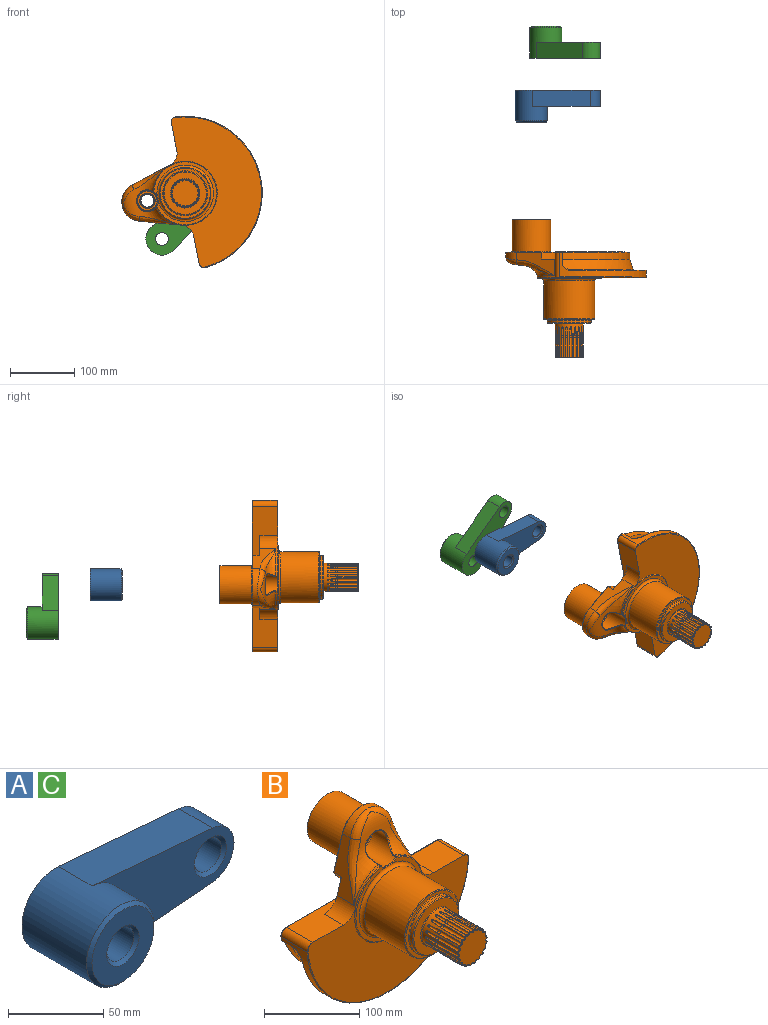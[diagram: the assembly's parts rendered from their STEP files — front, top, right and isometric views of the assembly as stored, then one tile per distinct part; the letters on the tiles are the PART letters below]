
ASSEMBLY  parts=3 mates=2
PART A: 12 faces, bbox 132.5x50x50 mm
  f0: plane 105.42x49.83mm, normal (0,-1,0), area 2885.2mm2, adj f1,f2,f3,f4,f9
  f1: cylinder r=25mm len=50mm, axis (0,1,0), area 5680.6mm2, adj f0,f2,f4,f7,f11
  f2: plane 89.38x25mm, normal (0.08,0,-1), area 2242.2mm2, adj f0,f1,f3,f7
  f3: cylinder r=17.5mm len=34.88mm, axis (0,1,0), area 1301.4mm2, adj f0,f2,f4,f7
  f4: plane 89.38x25mm, normal (0.08,0,1), area 2242.2mm2, adj f0,f1,f3,f7
  f5: cylinder r=10mm len=48mm, axis (0,1,0), area 3015.9mm2, adj f7,f10
  f6: cylinder r=10mm len=23mm, axis (0,1,0), area 1445.1mm2, adj f7,f9
  f7: plane 132.5x50mm, normal (0,1,0), area 4672.8mm2, adj f1,f2,f3,f4,f5,f6
  f8: plane 46x46mm, normal (0,-1,0), area 1209.5mm2, adj f10,f11
  f9: cone r=10mm half-angle=45deg, axis (0,-1,0), area 195.5mm2, adj f0,f6
  f10: cone r=10mm half-angle=45deg, axis (0,-1,0), area 195.5mm2, adj f5,f8
  f11: cone r=23mm half-angle=45deg, axis (0,1,0), area 426.5mm2, adj f1,f8
PART B: 359 faces, bbox 259.9x215.3x232.7 mm
  f0: cylinder r=22mm len=52mm, axis (0,-1,0), area 3266.6mm2, adj f52,f159,f162,f163,f166,f167,f170,f171
  f1: plane 42.73x42.73mm, normal (0,-1,0), area 1310mm2, adj f159,f160,f161,f162,f163,f164,f165,f166
  f2: cylinder r=50mm len=36.05mm, axis (0,1,0), area 156.2mm2, adj f19,f32,f44,f45
  f3: plane 237.43x92mm, normal (0,1,0), area 16224.2mm2, adj f60,f61,f62,f63,f64,f65,f66,f67
  f4: plane 98x96.6mm, normal (0,-1,0), area 1372.1mm2, adj f39,f40,f43,f44
  f5: plane 64.61x36.32mm, normal (-0.96,0,0.29), area 1116.4mm2, adj f6,f30,f31,f33,f34,f68,f71
  f6: cylinder r=30mm len=57.5mm, axis (0,-1,0), area 712.7mm2, adj f5,f7,f35,f69
  f7: plane 64.61x36.32mm, normal (0.96,0,0.29), area 1116.4mm2, adj f6,f30,f31,f32,f36,f68,f70
  f8: cylinder r=50mm len=36.05mm, axis (0,1,0), area 156.2mm2, adj f19,f33,f44,f48
  f9: plane 86.65x81.31mm, normal (0,1,0), area 2091.3mm2, adj f69,f70,f71,f72,f78
  f10: plane 223.43x39mm, normal (0,0,1), area 4957.1mm2, adj f11,f30,f32,f33,f37,f38,f65
  f11: plane 237.83x133.29mm, normal (0,-1,0), area 18403mm2, adj f10,f32,f33,f37,f38,f44,f53
  f12: cylinder r=120mm len=239.39mm, axis (0,-1,0), area 3826.2mm2, adj f27,f28,f37,f38,f53,f54,f55,f56
  f13: cylinder r=40mm len=80mm, axis (0,-1,0), area 14828.3mm2, adj f39,f49
  f14: plane 78x78mm, normal (0,-1,0), area 929.9mm2, adj f49,f50
  f15: cylinder r=34mm len=68mm, axis (0,-1,0), area 854.5mm2, adj f50,f51
  f16: plane 66x66mm, normal (0,-1,0), area 1759.3mm2, adj f51,f52
  f17: cylinder r=30mm len=60mm, axis (0,-1,0), area 9236.3mm2, adj f18,f78
  f18: plane 60x60mm, normal (0,1,0), area 1306.9mm2, adj f17,f76
  f19: revolved ~188.29x83.96mm, area 2110.2mm2, adj f2,f8,f34,f35,f36,f47
  f20: cylinder r=21mm len=42mm, axis (0,1,0), area 3034.8mm2, adj f76,f77
  f21: plane 40x40mm, normal (0,1,0), area 804.2mm2, adj f75,f77
  f22: cylinder r=11mm len=23mm, axis (0,1,0), area 1589.6mm2, adj f73,f75
  f23: cylinder r=16mm len=39mm, axis (0,1,0), area 2594.1mm2, adj f40,f41,f43,f45,f47,f48,f74
  f24: plane 30x30mm, normal (0,-1,0), area 254.5mm2, adj f73,f74
  f25: cone r=124mm half-angle=17deg, axis (0,-1,0), area 4998.2mm2, adj f27,f28,f29,f54,f57,f59
  f26: plane 230.56x89.48mm, normal (0,1,0), area 3734.6mm2, adj f56,f57
  f27: plane 20.74x2.73mm, normal (0.34,0,-0.94), area 45.7mm2, adj f12,f25,f29,f59,f60
  f28: plane 20.74x2.73mm, normal (-0.34,0,-0.94), area 45.7mm2, adj f12,f25,f29,f54,f64
  f29: cylinder r=124mm len=233.04mm, axis (0,-1,0), area 3332.9mm2, adj f25,f27,f28,f62
  f30: plane 134.16x33.71mm, normal (0,1,0), area 1873mm2, adj f5,f7,f10,f32,f33,f68
  f31: cylinder r=48.65mm len=83.48mm, axis (0,1,0), area 1003.4mm2, adj f5,f7,f68,f72
  f32: cylinder r=20mm len=28mm, axis (0,1,0), area 717.4mm2, adj f2,f7,f10,f11,f30
  f33: cylinder r=20mm len=28mm, axis (0,1,0), area 717.4mm2, adj f5,f8,f10,f11,f30
  f34: bspline ~68.35x27.48mm, area 558mm2, adj f5,f19,f35
  f35: bspline ~59.09x25.38mm, area 693.8mm2, adj f6,f19,f34,f36
  f36: bspline ~68.35x27.48mm, area 558mm2, adj f7,f19,f35
  f37: cylinder r=8mm len=39mm, axis (0,-1,0), area 510.3mm2, adj f10,f11,f12,f53,f67
  f38: cylinder r=8mm len=39mm, axis (0,-1,0), area 510.3mm2, adj f10,f11,f12,f53,f63
  f39: torus R=44mm, axis (0,-1,0), area 1631.2mm2, adj f4,f13,f41
  f40: torus R=17mm, axis (0,-1,0), area 11.8mm2, adj f4,f23,f41,f42
  f41: bspline ~12.15x1.91mm, area 13.8mm2, adj f23,f39,f40,f43
  f42: sphere r=1mm, area 1mm2, adj f40,f44,f45
  f43: torus R=17mm, axis (0,-1,0), area 11.8mm2, adj f4,f23,f41,f46
  f44: torus R=49mm, axis (0,-1,0), area 452.5mm2, adj f2,f4,f8,f11,f42,f46
  f45: cylinder r=1mm len=3mm, axis (0,1,0), area 3mm2, adj f2,f23,f42,f47
  f46: sphere r=1mm, area 1mm2, adj f43,f44,f48
  f47: bspline ~34.26x28.77mm, area 141.2mm2, adj f19,f23,f45,f48
  f48: cylinder r=1mm len=3mm, axis (0,-1,0), area 3mm2, adj f8,f23,f46,f47
  f49: torus R=39mm, axis (0,1,0), area 391.2mm2, adj f13,f14
  f50: torus R=35mm, axis (0,1,0), area 339.2mm2, adj f14,f15
  f51: torus R=33mm, axis (0,1,0), area 332mm2, adj f15,f16
  f52: torus R=23mm, axis (0,1,0), area 220.7mm2, adj f0,f16
  f53: torus R=119mm, axis (0,-1,0), area 569.8mm2, adj f11,f12,f37,f38
  f54: bspline ~21.98x16.93mm, area 3.9mm2, adj f12,f25,f28,f55
  f55: bspline ~11.03x3.76mm, area 8.9mm2, adj f12,f54,f56,f57
  f56: torus R=119mm, axis (0,-1,0), area 496.1mm2, adj f12,f26,f55,f58
  f57: torus R=129.74mm, axis (0,-1,0), area 370.6mm2, adj f25,f26,f55,f58
  f58: bspline ~9.6x3.23mm, area 8.9mm2, adj f12,f56,f57,f59
  f59: bspline ~21.98x16.93mm, area 3.9mm2, adj f12,f25,f27,f58
  f60: cylinder r=1mm len=4.01mm, axis (-0.94,0,-0.34), area 4.3mm2, adj f3,f27,f61,f62
  f61: torus R=119mm, axis (0,-1,0), area 6.6mm2, adj f3,f12,f60,f63
  f62: torus R=123mm, axis (0,-1,0), area 476.1mm2, adj f3,f29,f60,f64
  f63: torus R=7mm, axis (0,-1,0), area 19.7mm2, adj f3,f38,f61,f65
  f64: cylinder r=1mm len=4.01mm, axis (-0.94,0,0.34), area 4.3mm2, adj f3,f28,f62,f66
  f65: cylinder r=1mm len=223.43mm, axis (-1,0,0), area 351mm2, adj f3,f10,f63,f67
  f66: torus R=119mm, axis (0,-1,0), area 6.6mm2, adj f3,f12,f64,f67
  f67: torus R=7mm, axis (0,-1,0), area 19.7mm2, adj f3,f37,f65,f66
  f68: torus R=49.65mm, axis (0,-1,0), area 157.4mm2, adj f5,f7,f30,f31
  f69: torus R=29mm, axis (0,-1,0), area 119.3mm2, adj f6,f9,f70,f71
  f70: cylinder r=1mm len=43.86mm, axis (-0.29,0,0.96), area 71.1mm2, adj f7,f9,f69,f72
  f71: cylinder r=1mm len=43.86mm, axis (-0.29,0,-0.96), area 71.1mm2, adj f5,f9,f69,f72
  f72: torus R=47.65mm, axis (0,-1,0), area 155.7mm2, adj f9,f31,f70,f71
  f73: torus R=12mm, axis (0,1,0), area 112.2mm2, adj f22,f24
  f74: torus R=15mm, axis (0,1,0), area 154.3mm2, adj f23,f24
  f75: torus R=12mm, axis (0,1,0), area 112.2mm2, adj f21,f22
  f76: torus R=22mm, axis (0,1,0), area 210.8mm2, adj f18,f20
  f77: torus R=20mm, axis (0,1,0), area 203.7mm2, adj f20,f21
  f78: torus R=31mm, axis (0,-1,0), area 299.7mm2, adj f9,f17
  f79: revolved ~3.95x3.33mm, area 18.4mm2, adj f80,f82,f354,f355
  f80: cone r=1.06mm half-angle=3.8deg, axis (0,-1,0), area 50.6mm2, adj f79,f81,f356,f357
  f81: torus R=0.06mm, axis (0,1,0), area 2.6mm2, adj f80,f358
  f82: cylinder r=2mm len=30.28mm, axis (0,1,0), area 170.6mm2, adj f79,f351,f352,f353
  f83: revolved ~3.78x3.33mm, area 18.4mm2, adj f84,f86,f346,f347
  f84: cone r=1.06mm half-angle=3.8deg, axis (0,-1,0), area 50.6mm2, adj f83,f85,f348,f349
  f85: torus R=0.06mm, axis (0,1,0), area 2.6mm2, adj f84,f350
  f86: cylinder r=2mm len=30.28mm, axis (0,1,0), area 170.6mm2, adj f83,f343,f344,f345
  f87: revolved ~3.41x3.33mm, area 18.4mm2, adj f88,f90,f338,f339
  f88: cone r=1.06mm half-angle=3.8deg, axis (0,-1,0), area 50.6mm2, adj f87,f89,f340,f341
  f89: torus R=0.06mm, axis (0,1,0), area 2.6mm2, adj f88,f342
  f90: cylinder r=2mm len=30.28mm, axis (0,1,0), area 170.6mm2, adj f87,f335,f336,f337
  f91: revolved ~3.41x3.33mm, area 18.4mm2, adj f92,f94,f330,f331
  f92: cone r=1.06mm half-angle=3.8deg, axis (0,-1,0), area 50.6mm2, adj f91,f93,f332,f333
  f93: torus R=0.06mm, axis (0,1,0), area 2.6mm2, adj f92,f334
  f94: cylinder r=2mm len=30.28mm, axis (0,1,0), area 170.6mm2, adj f91,f327,f328,f329
  f95: revolved ~3.78x3.33mm, area 18.4mm2, adj f96,f98,f322,f323
  f96: cone r=1.06mm half-angle=3.8deg, axis (0,-1,0), area 50.6mm2, adj f95,f97,f324,f325
  f97: torus R=0.06mm, axis (0,1,0), area 2.6mm2, adj f96,f326
  f98: cylinder r=2mm len=30.28mm, axis (0,1,0), area 170.6mm2, adj f95,f319,f320,f321
  f99: revolved ~3.95x3.33mm, area 18.4mm2, adj f100,f102,f314,f315
  f100: cone r=1.06mm half-angle=3.8deg, axis (0,-1,0), area 50.6mm2, adj f99,f101,f316,f317
  f101: torus R=0.06mm, axis (0,1,0), area 2.6mm2, adj f100,f318
  f102: cylinder r=2mm len=30.28mm, axis (0,1,0), area 170.6mm2, adj f99,f311,f312,f313
  f103: revolved ~3.78x3.33mm, area 18.4mm2, adj f104,f106,f306,f307
  f104: cone r=1.06mm half-angle=3.8deg, axis (0,-1,0), area 50.6mm2, adj f103,f105,f308,f309
  f105: torus R=0.06mm, axis (0,1,0), area 2.6mm2, adj f104,f310
  f106: cylinder r=2mm len=30.28mm, axis (0,1,0), area 170.6mm2, adj f103,f303,f304,f305
  f107: revolved ~3.41x3.33mm, area 18.4mm2, adj f108,f110,f298,f299
  f108: cone r=1.06mm half-angle=3.8deg, axis (0,-1,0), area 50.6mm2, adj f107,f109,f300,f301
  f109: torus R=0.06mm, axis (0,1,0), area 2.6mm2, adj f108,f302
  f110: cylinder r=2mm len=30.28mm, axis (0,1,0), area 170.6mm2, adj f107,f295,f296,f297
  f111: revolved ~3.41x3.33mm, area 18.4mm2, adj f112,f114,f290,f291
  f112: cone r=1.06mm half-angle=3.8deg, axis (0,-1,0), area 50.6mm2, adj f111,f113,f292,f293
  f113: torus R=0.06mm, axis (0,1,0), area 2.6mm2, adj f112,f294
  f114: cylinder r=2mm len=30.28mm, axis (0,1,0), area 170.6mm2, adj f111,f287,f288,f289
  f115: revolved ~3.78x3.33mm, area 18.4mm2, adj f116,f118,f282,f283
  f116: cone r=1.06mm half-angle=3.8deg, axis (0,-1,0), area 50.6mm2, adj f115,f117,f284,f285
  f117: torus R=0.06mm, axis (0,1,0), area 2.6mm2, adj f116,f286
  f118: cylinder r=2mm len=30.28mm, axis (0,1,0), area 170.6mm2, adj f115,f279,f280,f281
  f119: revolved ~3.95x3.33mm, area 18.4mm2, adj f120,f122,f274,f275
  f120: cone r=1.06mm half-angle=3.8deg, axis (0,-1,0), area 50.6mm2, adj f119,f121,f276,f277
  f121: torus R=0.06mm, axis (0,1,0), area 2.6mm2, adj f120,f278
  f122: cylinder r=2mm len=30.28mm, axis (0,1,0), area 170.6mm2, adj f119,f271,f272,f273
  f123: revolved ~3.78x3.33mm, area 18.4mm2, adj f124,f126,f266,f267
  f124: cone r=1.06mm half-angle=3.8deg, axis (0,-1,0), area 50.6mm2, adj f123,f125,f268,f269
  f125: torus R=0.06mm, axis (0,1,0), area 2.6mm2, adj f124,f270
  f126: cylinder r=2mm len=30.28mm, axis (0,1,0), area 170.6mm2, adj f123,f263,f264,f265
  f127: revolved ~3.41x3.33mm, area 18.4mm2, adj f128,f130,f258,f259
  f128: cone r=1.06mm half-angle=3.8deg, axis (0,-1,0), area 50.6mm2, adj f127,f129,f260,f261
  f129: torus R=0.06mm, axis (0,1,0), area 2.6mm2, adj f128,f262
  f130: cylinder r=2mm len=30.28mm, axis (0,1,0), area 170.6mm2, adj f127,f255,f256,f257
  f131: revolved ~3.41x3.33mm, area 18.4mm2, adj f132,f134,f250,f251
  f132: cone r=1.06mm half-angle=3.8deg, axis (0,-1,0), area 50.6mm2, adj f131,f133,f252,f253
  f133: torus R=0.06mm, axis (0,1,0), area 2.6mm2, adj f132,f254
  f134: cylinder r=2mm len=30.28mm, axis (0,1,0), area 170.6mm2, adj f131,f247,f248,f249
  f135: revolved ~3.78x3.33mm, area 18.4mm2, adj f136,f138,f242,f243
  f136: cone r=1.06mm half-angle=3.8deg, axis (0,-1,0), area 50.6mm2, adj f135,f137,f244,f245
  f137: torus R=0.06mm, axis (0,1,0), area 2.6mm2, adj f136,f246
  f138: cylinder r=2mm len=30.28mm, axis (0,1,0), area 170.6mm2, adj f135,f239,f240,f241
  f139: revolved ~3.95x3.33mm, area 18.4mm2, adj f140,f142,f234,f235
  f140: cone r=1.06mm half-angle=3.8deg, axis (0,-1,0), area 50.6mm2, adj f139,f141,f236,f237
  f141: torus R=0.06mm, axis (0,1,0), area 2.6mm2, adj f140,f238
  f142: cylinder r=2mm len=30.28mm, axis (0,1,0), area 170.6mm2, adj f139,f231,f232,f233
  f143: revolved ~3.78x3.33mm, area 18.4mm2, adj f144,f146,f226,f227
  f144: cone r=1.06mm half-angle=3.8deg, axis (0,-1,0), area 50.6mm2, adj f143,f145,f228,f229
  f145: torus R=0.06mm, axis (0,1,0), area 2.6mm2, adj f144,f230
  f146: cylinder r=2mm len=30.28mm, axis (0,1,0), area 170.6mm2, adj f143,f223,f224,f225
  f147: revolved ~3.41x3.33mm, area 18.4mm2, adj f148,f150,f218,f219
  f148: cone r=1.06mm half-angle=3.8deg, axis (0,-1,0), area 50.6mm2, adj f147,f149,f220,f221
  f149: torus R=0.06mm, axis (0,1,0), area 2.6mm2, adj f148,f222
  f150: cylinder r=2mm len=30.28mm, axis (0,1,0), area 170.6mm2, adj f147,f215,f216,f217
  f151: revolved ~3.41x3.33mm, area 18.4mm2, adj f152,f154,f210,f211
  f152: cone r=1.06mm half-angle=3.8deg, axis (0,-1,0), area 50.6mm2, adj f151,f153,f212,f213
  f153: torus R=0.06mm, axis (0,1,0), area 2.6mm2, adj f152,f214
  f154: cylinder r=2mm len=30.28mm, axis (0,1,0), area 170.6mm2, adj f151,f207,f208,f209
  f155: revolved ~3.78x3.33mm, area 18.4mm2, adj f156,f158,f202,f203
  f156: cone r=1.06mm half-angle=3.8deg, axis (0,-1,0), area 50.6mm2, adj f155,f157,f204,f205
  f157: torus R=0.06mm, axis (0,1,0), area 2.6mm2, adj f156,f206
  f158: cylinder r=2mm len=30.28mm, axis (0,1,0), area 170.6mm2, adj f155,f199,f200,f201
  f159: cone r=21.5mm half-angle=26.6deg, axis (0,1,0), area 2.6mm2, adj f0,f1,f160,f161,f280,f289
  f160: cone r=2.5mm half-angle=26.6deg, axis (0,-1,0), area 6.7mm2, adj f1,f159,f162,f279,f280,f281
  f161: cone r=2.5mm half-angle=26.6deg, axis (0,-1,0), area 6.7mm2, adj f1,f159,f163,f287,f288,f289
  f162: cone r=21.5mm half-angle=26.6deg, axis (0,1,0), area 2.6mm2, adj f0,f1,f160,f164,f272,f281
  f163: cone r=21.5mm half-angle=26.6deg, axis (0,1,0), area 2.6mm2, adj f0,f1,f161,f165,f288,f297
  f164: cone r=2.5mm half-angle=26.6deg, axis (0,-1,0), area 6.7mm2, adj f1,f162,f166,f271,f272,f273
  f165: cone r=2.5mm half-angle=26.6deg, axis (0,-1,0), area 6.7mm2, adj f1,f163,f167,f295,f296,f297
  f166: cone r=21.5mm half-angle=26.6deg, axis (0,1,0), area 2.6mm2, adj f0,f1,f164,f168,f264,f273
  f167: cone r=21.5mm half-angle=26.6deg, axis (0,1,0), area 2.6mm2, adj f0,f1,f165,f169,f296,f305
  f168: cone r=2.5mm half-angle=26.6deg, axis (0,-1,0), area 6.7mm2, adj f1,f166,f170,f263,f264,f265
  f169: cone r=2.5mm half-angle=26.6deg, axis (0,-1,0), area 6.7mm2, adj f1,f167,f171,f303,f304,f305
  f170: cone r=21.5mm half-angle=26.6deg, axis (0,1,0), area 2.6mm2, adj f0,f1,f168,f172,f256,f265
  f171: cone r=21.5mm half-angle=26.6deg, axis (0,1,0), area 2.6mm2, adj f0,f1,f169,f173,f304,f313
  f172: cone r=2.5mm half-angle=26.6deg, axis (0,-1,0), area 6.7mm2, adj f1,f170,f174,f255,f256,f257
  f173: cone r=2.5mm half-angle=26.6deg, axis (0,-1,0), area 6.7mm2, adj f1,f171,f175,f311,f312,f313
  f174: cone r=21.5mm half-angle=26.6deg, axis (0,1,0), area 2.6mm2, adj f0,f1,f172,f176,f248,f257
  f175: cone r=21.5mm half-angle=26.6deg, axis (0,1,0), area 2.6mm2, adj f0,f1,f173,f177,f312,f321
  f176: cone r=2.5mm half-angle=26.6deg, axis (0,-1,0), area 6.7mm2, adj f1,f174,f178,f247,f248,f249
  f177: cone r=2.5mm half-angle=26.6deg, axis (0,-1,0), area 6.7mm2, adj f1,f175,f179,f319,f320,f321
  f178: cone r=21.5mm half-angle=26.6deg, axis (0,1,0), area 2.6mm2, adj f0,f1,f176,f180,f240,f249
  f179: cone r=21.5mm half-angle=26.6deg, axis (0,1,0), area 2.6mm2, adj f0,f1,f177,f181,f320,f329
  f180: cone r=2.5mm half-angle=26.6deg, axis (0,-1,0), area 6.7mm2, adj f1,f178,f182,f239,f240,f241
  f181: cone r=2.5mm half-angle=26.6deg, axis (0,-1,0), area 6.7mm2, adj f1,f179,f183,f327,f328,f329
  f182: cone r=21.5mm half-angle=26.6deg, axis (0,1,0), area 2.6mm2, adj f0,f1,f180,f184,f232,f241
  f183: cone r=21.5mm half-angle=26.6deg, axis (0,1,0), area 2.6mm2, adj f0,f1,f181,f185,f328,f337
  f184: cone r=2.5mm half-angle=26.6deg, axis (0,-1,0), area 6.7mm2, adj f1,f182,f186,f231,f232,f233
  f185: cone r=2.5mm half-angle=26.6deg, axis (0,-1,0), area 6.7mm2, adj f1,f183,f187,f335,f336,f337
  f186: cone r=21.5mm half-angle=26.6deg, axis (0,1,0), area 2.6mm2, adj f0,f1,f184,f188,f224,f233
  f187: cone r=21.5mm half-angle=26.6deg, axis (0,1,0), area 2.6mm2, adj f0,f1,f185,f189,f336,f345
  f188: cone r=2.5mm half-angle=26.6deg, axis (0,-1,0), area 6.7mm2, adj f1,f186,f190,f223,f224,f225
  f189: cone r=2.5mm half-angle=26.6deg, axis (0,-1,0), area 6.7mm2, adj f1,f187,f191,f343,f344,f345
  f190: cone r=21.5mm half-angle=26.6deg, axis (0,1,0), area 2.6mm2, adj f0,f1,f188,f192,f216,f225
  f191: cone r=21.5mm half-angle=26.6deg, axis (0,1,0), area 2.6mm2, adj f0,f1,f189,f193,f344,f353
  f192: cone r=2.5mm half-angle=26.6deg, axis (0,-1,0), area 6.7mm2, adj f1,f190,f194,f215,f216,f217
  f193: cone r=2.5mm half-angle=26.6deg, axis (0,-1,0), area 6.7mm2, adj f1,f191,f195,f351,f352,f353
  f194: cone r=21.5mm half-angle=26.6deg, axis (0,1,0), area 2.6mm2, adj f0,f1,f192,f196,f208,f217
  f195: cone r=21.5mm half-angle=26.6deg, axis (0,1,0), area 2.6mm2, adj f0,f1,f193,f197,f201,f352
  f196: cone r=2.5mm half-angle=26.6deg, axis (0,-1,0), area 6.7mm2, adj f1,f194,f198,f207,f208,f209
  f197: cone r=2.5mm half-angle=26.6deg, axis (0,-1,0), area 6.7mm2, adj f1,f195,f198,f199,f200,f201
  f198: cone r=21.5mm half-angle=26.6deg, axis (0,1,0), area 2.6mm2, adj f0,f1,f196,f197,f200,f209
  f199: torus R=2.25mm, axis (0,1,0), area 0.7mm2, adj f158,f197,f200,f201
  f200: cylinder r=0.25mm len=30.48mm, axis (0,-1,0), area 11.5mm2, adj f0,f158,f197,f198,f199,f202
  f201: cylinder r=0.25mm len=30.48mm, axis (0,1,0), area 11.5mm2, adj f0,f158,f195,f197,f199,f203
  f202: bspline ~4.78x0.47mm, area 1.3mm2, adj f0,f155,f200,f204
  f203: bspline ~6.5x0.57mm, area 1.3mm2, adj f0,f155,f201,f205
  f204: bspline ~15.29x1.26mm, area 4.5mm2, adj f0,f156,f202,f206
  f205: bspline ~16.73x1.3mm, area 4.5mm2, adj f0,f156,f203,f206
  f206: bspline ~2.47x1.43mm, area 1.2mm2, adj f0,f157,f204,f205
  f207: torus R=2.25mm, axis (0,1,0), area 0.7mm2, adj f154,f196,f208,f209
  f208: cylinder r=0.25mm len=30.48mm, axis (0,-1,0), area 11.5mm2, adj f0,f154,f194,f196,f207,f210
  f209: cylinder r=0.25mm len=30.48mm, axis (0,1,0), area 11.5mm2, adj f0,f154,f196,f198,f207,f211
  f210: bspline ~4.78x0.46mm, area 1.3mm2, adj f0,f151,f208,f212
  f211: bspline ~6.5x0.51mm, area 1.3mm2, adj f0,f151,f209,f213
  f212: bspline ~15.29x1.11mm, area 4.5mm2, adj f0,f152,f210,f214
  f213: bspline ~16.73x1.14mm, area 4.5mm2, adj f0,f152,f211,f214
  f214: bspline ~2.1x1.53mm, area 1.2mm2, adj f0,f153,f212,f213
  f215: torus R=2.25mm, axis (0,1,0), area 0.7mm2, adj f150,f192,f216,f217
  f216: cylinder r=0.25mm len=30.48mm, axis (0,-1,0), area 11.5mm2, adj f0,f150,f190,f192,f215,f218
  f217: cylinder r=0.25mm len=30.48mm, axis (0,1,0), area 11.5mm2, adj f0,f150,f192,f194,f215,f219
  f218: bspline ~4.78x0.41mm, area 1.3mm2, adj f0,f147,f216,f220
  f219: bspline ~6.5x0.61mm, area 1.3mm2, adj f0,f147,f217,f221
  f220: bspline ~15.29x1.06mm, area 4.5mm2, adj f0,f148,f218,f222
  f221: bspline ~16.73x1.18mm, area 4.5mm2, adj f0,f148,f219,f222
  f222: bspline ~2.1x1.53mm, area 1.2mm2, adj f0,f149,f220,f221
  f223: torus R=2.25mm, axis (0,1,0), area 0.7mm2, adj f146,f188,f224,f225
  f224: cylinder r=0.25mm len=30.48mm, axis (0,-1,0), area 11.5mm2, adj f0,f146,f186,f188,f223,f226
  f225: cylinder r=0.25mm len=30.48mm, axis (0,1,0), area 11.5mm2, adj f0,f146,f188,f190,f223,f227
  f226: bspline ~4.78x0.39mm, area 1.3mm2, adj f0,f143,f224,f228
  f227: bspline ~6.5x0.65mm, area 1.3mm2, adj f0,f143,f225,f229
  f228: bspline ~15.29x1.21mm, area 4.5mm2, adj f0,f144,f226,f230
  f229: bspline ~16.73x1.35mm, area 4.5mm2, adj f0,f144,f227,f230
  f230: bspline ~2.47x1.43mm, area 1.2mm2, adj f0,f145,f228,f229
  f231: torus R=2.25mm, axis (0,1,0), area 0.7mm2, adj f142,f184,f232,f233
  f232: cylinder r=0.25mm len=30.48mm, axis (0,-1,0), area 11.5mm2, adj f0,f142,f182,f184,f231,f234
  f233: cylinder r=0.25mm len=30.48mm, axis (0,1,0), area 11.5mm2, adj f0,f142,f184,f186,f231,f235
  f234: bspline ~4.78x0.43mm, area 1.3mm2, adj f0,f139,f232,f236
  f235: bspline ~6.5x0.63mm, area 1.3mm2, adj f0,f139,f233,f237
  f236: bspline ~15.29x1.29mm, area 4.5mm2, adj f0,f140,f234,f238
  f237: bspline ~16.73x1.39mm, area 4.5mm2, adj f0,f140,f235,f238
  f238: bspline ~2.6x1.43mm, area 1.2mm2, adj f0,f141,f236,f237
  f239: torus R=2.25mm, axis (0,1,0), area 0.7mm2, adj f138,f180,f240,f241
  f240: cylinder r=0.25mm len=30.48mm, axis (0,-1,0), area 11.5mm2, adj f0,f138,f178,f180,f239,f242
  f241: cylinder r=0.25mm len=30.48mm, axis (0,1,0), area 11.5mm2, adj f0,f138,f180,f182,f239,f243
  f242: bspline ~7.03x0.47mm, area 1.3mm2, adj f0,f135,f240,f244
  f243: bspline ~6.5x0.57mm, area 1.3mm2, adj f0,f135,f241,f245
  f244: bspline ~15.29x1.26mm, area 4.5mm2, adj f0,f136,f242,f246
  f245: bspline ~16.73x1.3mm, area 4.5mm2, adj f0,f136,f243,f246
  f246: bspline ~2.47x1.43mm, area 1.2mm2, adj f0,f137,f244,f245
  f247: torus R=2.25mm, axis (0,1,0), area 0.7mm2, adj f134,f176,f248,f249
  f248: cylinder r=0.25mm len=30.48mm, axis (0,-1,0), area 11.5mm2, adj f0,f134,f174,f176,f247,f250
  f249: cylinder r=0.25mm len=30.48mm, axis (0,1,0), area 11.5mm2, adj f0,f134,f176,f178,f247,f251
  f250: bspline ~4.78x0.46mm, area 1.3mm2, adj f0,f131,f248,f252
  f251: bspline ~6.5x0.51mm, area 1.3mm2, adj f0,f131,f249,f253
  f252: bspline ~15.29x1.11mm, area 4.5mm2, adj f0,f132,f250,f254
  f253: bspline ~16.73x1.14mm, area 4.5mm2, adj f0,f132,f251,f254
  f254: bspline ~2.1x1.53mm, area 1.2mm2, adj f0,f133,f252,f253
  f255: torus R=2.25mm, axis (0,1,0), area 0.7mm2, adj f130,f172,f256,f257
  f256: cylinder r=0.25mm len=30.48mm, axis (0,-1,0), area 11.5mm2, adj f0,f130,f170,f172,f255,f258
  f257: cylinder r=0.25mm len=30.48mm, axis (0,1,0), area 11.5mm2, adj f0,f130,f172,f174,f255,f259
  f258: bspline ~4.78x0.41mm, area 1.3mm2, adj f0,f127,f256,f260
  f259: bspline ~6.5x0.61mm, area 1.3mm2, adj f0,f127,f257,f261
  f260: bspline ~15.29x1.06mm, area 4.5mm2, adj f0,f128,f258,f262
  f261: bspline ~16.73x1.18mm, area 4.5mm2, adj f0,f128,f259,f262
  f262: bspline ~2.1x1.53mm, area 1.2mm2, adj f0,f129,f260,f261
  f263: torus R=2.25mm, axis (0,1,0), area 0.7mm2, adj f126,f168,f264,f265
  f264: cylinder r=0.25mm len=30.48mm, axis (0,-1,0), area 11.5mm2, adj f0,f126,f166,f168,f263,f266
  f265: cylinder r=0.25mm len=30.48mm, axis (0,1,0), area 11.5mm2, adj f0,f126,f168,f170,f263,f267
  f266: bspline ~4.78x0.39mm, area 1.3mm2, adj f0,f123,f264,f268
  f267: bspline ~6.5x0.65mm, area 1.3mm2, adj f0,f123,f265,f269
  f268: bspline ~15.29x1.21mm, area 4.5mm2, adj f0,f124,f266,f270
  f269: bspline ~16.73x1.35mm, area 4.5mm2, adj f0,f124,f267,f270
  f270: bspline ~2.47x1.43mm, area 1.2mm2, adj f0,f125,f268,f269
  f271: torus R=2.25mm, axis (0,1,0), area 0.7mm2, adj f122,f164,f272,f273
  f272: cylinder r=0.25mm len=30.48mm, axis (0,-1,0), area 11.5mm2, adj f0,f122,f162,f164,f271,f274
  f273: cylinder r=0.25mm len=30.48mm, axis (0,1,0), area 11.5mm2, adj f0,f122,f164,f166,f271,f275
  f274: bspline ~4.78x0.43mm, area 1.3mm2, adj f0,f119,f272,f276
  f275: bspline ~6.5x0.63mm, area 1.3mm2, adj f0,f119,f273,f277
  f276: bspline ~15.29x1.29mm, area 4.5mm2, adj f0,f120,f274,f278
  f277: bspline ~16.73x1.39mm, area 4.5mm2, adj f0,f120,f275,f278
  f278: bspline ~2.6x1.43mm, area 1.2mm2, adj f0,f121,f276,f277
  f279: torus R=2.25mm, axis (0,1,0), area 0.7mm2, adj f118,f160,f280,f281
  f280: cylinder r=0.25mm len=30.48mm, axis (0,-1,0), area 11.5mm2, adj f0,f118,f159,f160,f279,f282
  f281: cylinder r=0.25mm len=30.48mm, axis (0,1,0), area 11.5mm2, adj f0,f118,f160,f162,f279,f283
  f282: bspline ~4.78x0.47mm, area 1.3mm2, adj f0,f115,f280,f284
  f283: bspline ~6.5x0.57mm, area 1.3mm2, adj f0,f115,f281,f285
  f284: bspline ~15.29x1.26mm, area 4.5mm2, adj f0,f116,f282,f286
  f285: bspline ~16.73x1.3mm, area 4.5mm2, adj f0,f116,f283,f286
  f286: bspline ~2.47x1.43mm, area 1.2mm2, adj f0,f117,f284,f285
  f287: torus R=2.25mm, axis (0,1,0), area 0.7mm2, adj f114,f161,f288,f289
  f288: cylinder r=0.25mm len=30.48mm, axis (0,-1,0), area 11.5mm2, adj f0,f114,f161,f163,f287,f290
  f289: cylinder r=0.25mm len=30.48mm, axis (0,1,0), area 11.5mm2, adj f0,f114,f159,f161,f287,f291
  f290: bspline ~4.78x0.46mm, area 1.3mm2, adj f0,f111,f288,f292
  f291: bspline ~6.5x0.51mm, area 1.3mm2, adj f0,f111,f289,f293
  f292: bspline ~15.29x1.11mm, area 4.5mm2, adj f0,f112,f290,f294
  f293: bspline ~16.73x1.14mm, area 4.5mm2, adj f0,f112,f291,f294
  f294: bspline ~2.1x1.53mm, area 1.2mm2, adj f0,f113,f292,f293
  f295: torus R=2.25mm, axis (0,1,0), area 0.7mm2, adj f110,f165,f296,f297
  f296: cylinder r=0.25mm len=30.48mm, axis (0,-1,0), area 11.5mm2, adj f0,f110,f165,f167,f295,f298
  f297: cylinder r=0.25mm len=30.48mm, axis (0,1,0), area 11.5mm2, adj f0,f110,f163,f165,f295,f299
  f298: bspline ~4.78x0.41mm, area 1.3mm2, adj f0,f107,f296,f300
  f299: bspline ~6.5x0.61mm, area 1.3mm2, adj f0,f107,f297,f301
  f300: bspline ~15.29x1.06mm, area 4.5mm2, adj f0,f108,f298,f302
  f301: bspline ~16.73x1.18mm, area 4.5mm2, adj f0,f108,f299,f302
  f302: bspline ~2.1x1.53mm, area 1.2mm2, adj f0,f109,f300,f301
  f303: torus R=2.25mm, axis (0,1,0), area 0.7mm2, adj f106,f169,f304,f305
  f304: cylinder r=0.25mm len=30.48mm, axis (0,-1,0), area 11.5mm2, adj f0,f106,f169,f171,f303,f306
  f305: cylinder r=0.25mm len=30.48mm, axis (0,1,0), area 11.5mm2, adj f0,f106,f167,f169,f303,f307
  f306: bspline ~7.03x0.39mm, area 1.3mm2, adj f0,f103,f304,f308
  f307: bspline ~6.5x0.65mm, area 1.3mm2, adj f0,f103,f305,f309
  f308: bspline ~15.29x1.21mm, area 4.5mm2, adj f0,f104,f306,f310
  f309: bspline ~16.73x1.35mm, area 4.5mm2, adj f0,f104,f307,f310
  f310: bspline ~2.47x1.43mm, area 1.2mm2, adj f0,f105,f308,f309
  f311: torus R=2.25mm, axis (0,1,0), area 0.7mm2, adj f102,f173,f312,f313
  f312: cylinder r=0.25mm len=30.48mm, axis (0,-1,0), area 11.5mm2, adj f0,f102,f173,f175,f311,f314
  f313: cylinder r=0.25mm len=30.48mm, axis (0,1,0), area 11.5mm2, adj f0,f102,f171,f173,f311,f315
  f314: bspline ~4.78x0.43mm, area 1.3mm2, adj f0,f99,f312,f316
  f315: bspline ~6.5x0.63mm, area 1.3mm2, adj f0,f99,f313,f317
  f316: bspline ~15.29x1.29mm, area 4.5mm2, adj f0,f100,f314,f318
  f317: bspline ~16.73x1.39mm, area 4.5mm2, adj f0,f100,f315,f318
  f318: bspline ~2.6x1.43mm, area 1.2mm2, adj f0,f101,f316,f317
  f319: torus R=2.25mm, axis (0,1,0), area 0.7mm2, adj f98,f177,f320,f321
  f320: cylinder r=0.25mm len=30.48mm, axis (0,-1,0), area 11.5mm2, adj f0,f98,f177,f179,f319,f322
  f321: cylinder r=0.25mm len=30.48mm, axis (0,1,0), area 11.5mm2, adj f0,f98,f175,f177,f319,f323
  f322: bspline ~4.78x0.47mm, area 1.3mm2, adj f0,f95,f320,f324
  f323: bspline ~6.5x0.57mm, area 1.3mm2, adj f0,f95,f321,f325
  f324: bspline ~15.29x1.26mm, area 4.5mm2, adj f0,f96,f322,f326
  f325: bspline ~16.73x1.3mm, area 4.5mm2, adj f0,f96,f323,f326
  f326: bspline ~2.47x1.43mm, area 1.2mm2, adj f0,f97,f324,f325
  f327: torus R=2.25mm, axis (0,1,0), area 0.7mm2, adj f94,f181,f328,f329
  f328: cylinder r=0.25mm len=30.48mm, axis (0,-1,0), area 11.5mm2, adj f0,f94,f181,f183,f327,f330
  f329: cylinder r=0.25mm len=30.48mm, axis (0,1,0), area 11.5mm2, adj f0,f94,f179,f181,f327,f331
  f330: bspline ~6.52x0.43mm, area 1.3mm2, adj f0,f91,f328,f332
  f331: bspline ~6.5x0.51mm, area 1.3mm2, adj f0,f91,f329,f333
  f332: bspline ~15.29x1.11mm, area 4.5mm2, adj f0,f92,f330,f334
  f333: bspline ~16.73x1.14mm, area 4.5mm2, adj f0,f92,f331,f334
  f334: bspline ~2.1x1.53mm, area 1.2mm2, adj f0,f93,f332,f333
  f335: torus R=2.25mm, axis (0,1,0), area 0.7mm2, adj f90,f185,f336,f337
  f336: cylinder r=0.25mm len=30.48mm, axis (0,-1,0), area 11.5mm2, adj f0,f90,f185,f187,f335,f338
  f337: cylinder r=0.25mm len=30.48mm, axis (0,1,0), area 11.5mm2, adj f0,f90,f183,f185,f335,f339
  f338: bspline ~4.78x0.41mm, area 1.3mm2, adj f0,f87,f336,f340
  f339: bspline ~6.5x0.61mm, area 1.3mm2, adj f0,f87,f337,f341
  f340: bspline ~15.29x1.06mm, area 4.5mm2, adj f0,f88,f338,f342
  f341: bspline ~16.73x1.18mm, area 4.5mm2, adj f0,f88,f339,f342
  f342: bspline ~2.1x1.53mm, area 1.2mm2, adj f0,f89,f340,f341
  f343: torus R=2.25mm, axis (0,1,0), area 0.7mm2, adj f86,f189,f344,f345
  f344: cylinder r=0.25mm len=30.48mm, axis (0,-1,0), area 11.5mm2, adj f0,f86,f189,f191,f343,f346
  f345: cylinder r=0.25mm len=30.48mm, axis (0,1,0), area 11.5mm2, adj f0,f86,f187,f189,f343,f347
  f346: bspline ~7.03x0.39mm, area 1.3mm2, adj f0,f83,f344,f348
  f347: bspline ~6.5x0.65mm, area 1.3mm2, adj f0,f83,f345,f349
  f348: bspline ~15.29x1.21mm, area 4.5mm2, adj f0,f84,f346,f350
  f349: bspline ~16.73x1.35mm, area 4.5mm2, adj f0,f84,f347,f350
  f350: bspline ~2.47x1.43mm, area 1.2mm2, adj f0,f85,f348,f349
  f351: torus R=2.25mm, axis (0,1,0), area 0.7mm2, adj f82,f193,f352,f353
  f352: cylinder r=0.25mm len=30.48mm, axis (0,-1,0), area 11.5mm2, adj f0,f82,f193,f195,f351,f354
  f353: cylinder r=0.25mm len=30.48mm, axis (0,1,0), area 11.5mm2, adj f0,f82,f191,f193,f351,f355
  f354: bspline ~4.78x0.43mm, area 1.3mm2, adj f0,f79,f352,f356
  f355: bspline ~6.5x0.63mm, area 1.3mm2, adj f0,f79,f353,f357
  f356: bspline ~15.29x1.29mm, area 4.5mm2, adj f0,f80,f354,f358
  f357: bspline ~16.73x1.39mm, area 4.5mm2, adj f0,f80,f355,f358
  f358: bspline ~2.6x1.43mm, area 1.2mm2, adj f0,f81,f356,f357
PART C: same geometry as A
PLACE A at identity fixed
PLACE B rot(axis=(0,-1,0),101.2deg) t=(58.86,-292.18,11.65)mm
PLACE C rot(axis=(-0.94,0,-0.35),180deg) t=(22.59,50,-59.63)mm
MATE cylindrical B.f17 <-> A.f1  axis (0,-1,0) through (0,-226.68,0)mm
MATE revolute C.f3 <-> A.f3  axis (0,-1,0) through (90,50,0)mm
